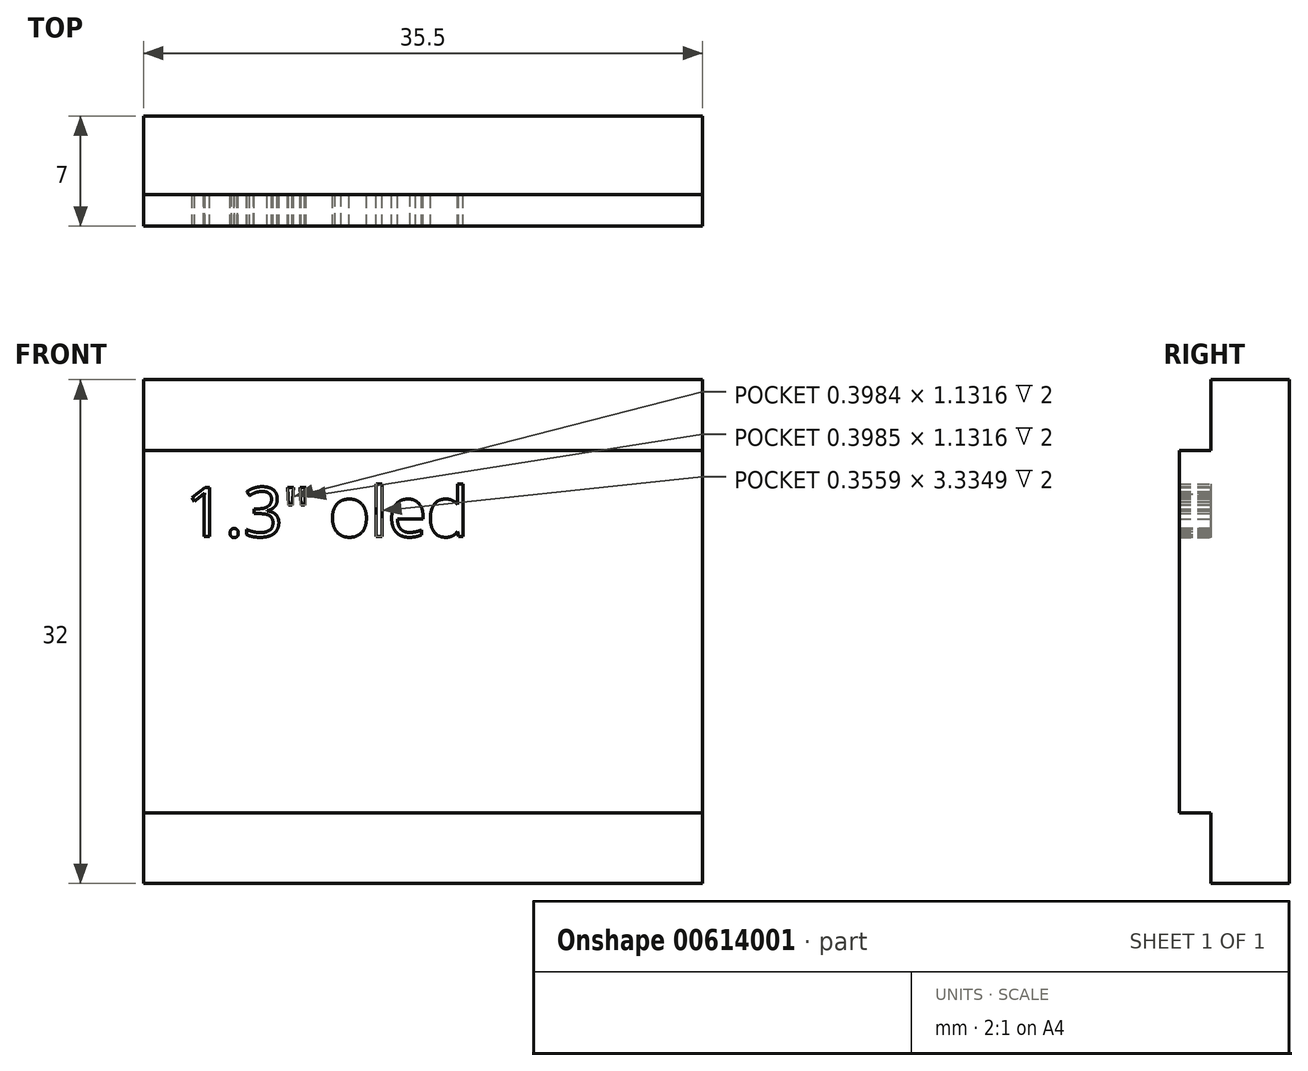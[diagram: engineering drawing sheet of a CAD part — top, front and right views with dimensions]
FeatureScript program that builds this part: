
annotation { "Feature Type Name" : "Feature", "Feature Type Description" : "" }
export const myFeature = defineFeature(function(context is Context, id is Id, definition is map)
    precondition{}
    {
        {
            var Q0;
            Q0=qCreatedBy(makeId("Front.planeOp"),FACE);
            var sketch = newSketch(context, id + "F0", { "sketchPlane" : qUnion([Q0])});
            skLineSegment(sketch, "E0.bottom", {"start": v(-17.75, 11.5) * mm, "end": v(17.75, 11.5) * mm});
            skLineSegment(sketch, "E0.top", {"start": v(-17.75, -11.5) * mm, "end": v(17.75, -11.5) * mm});
            skLineSegment(sketch, "E0.left", {"start": v(-17.75, 11.5) * mm, "end": v(-17.75, -11.5) * mm});
            skLineSegment(sketch, "E0.right", {"start": v(17.75, 11.5) * mm, "end": v(17.75, -11.5) * mm});
            skPoint(sketch, "E0.middle", {"position": v(0, 0) * mm});
            skText(sketch, "E1", { "text": "1.3\" oled \n\n", "fontName": "OpenSans-Regular.ttf"});
            const initialGuessF0  = {"E1": [-0.01509, 0.00603, 1, 0, 0.00316]};
            skSetInitialGuess(sketch, initialGuessF0);
            skSolve(sketch);
        }
        {
            var Q0;
            Q0=makeQuery(id+"F0.imprint","IMPRINT",FACE,{"disambiguationData":[TD([[makeQuery(id+"F0.imprint","IMPRINT",EDGE,{"derivedFrom":sQuery(id+"F0.wireOp",EDGE,"E0.bottom")}),-1.0]])]});
            extrude(context, id + "F1", {"entities" : qUnion([Q0]), "depth" : 2 * mm, "offsetDistance" : 25 * mm});
        }
        {
            var Q0;
            Q0=qCreatedBy(makeId("Front.planeOp"),FACE);
            var sketch = newSketch(context, id + "F2", { "sketchPlane" : qUnion([Q0])});
            skLineSegment(sketch, "E2.bottom", {"start": v(17.75, 16) * mm, "end": v(-17.75, 16) * mm});
            skLineSegment(sketch, "E2.top", {"start": v(17.75, -16) * mm, "end": v(-17.75, -16) * mm});
            skLineSegment(sketch, "E2.left", {"start": v(17.75, 16) * mm, "end": v(17.75, -16) * mm});
            skLineSegment(sketch, "E2.right", {"start": v(-17.75, 16) * mm, "end": v(-17.75, -16) * mm});
            skPoint(sketch, "E2.middle", {"position": v(0, 0) * mm});
            skSolve(sketch);
        }
        {
            var Q0;
            Q0=makeQuery(id+"F2.imprint","IMPRINT",FACE,{"disambiguationData":[TD([[makeQuery(id+"F2.imprint","IMPRINT",EDGE,{"derivedFrom":sQuery(id+"F2.wireOp",EDGE,"E2.bottom")}),1.0]])]});
            extrude(context, id + "F3", {"entities" : qUnion([Q0]), "operationType" : NewBodyOperationType.ADD, "depth" : -5 * mm, "offsetDistance" : 25 * mm});
        }
    });
